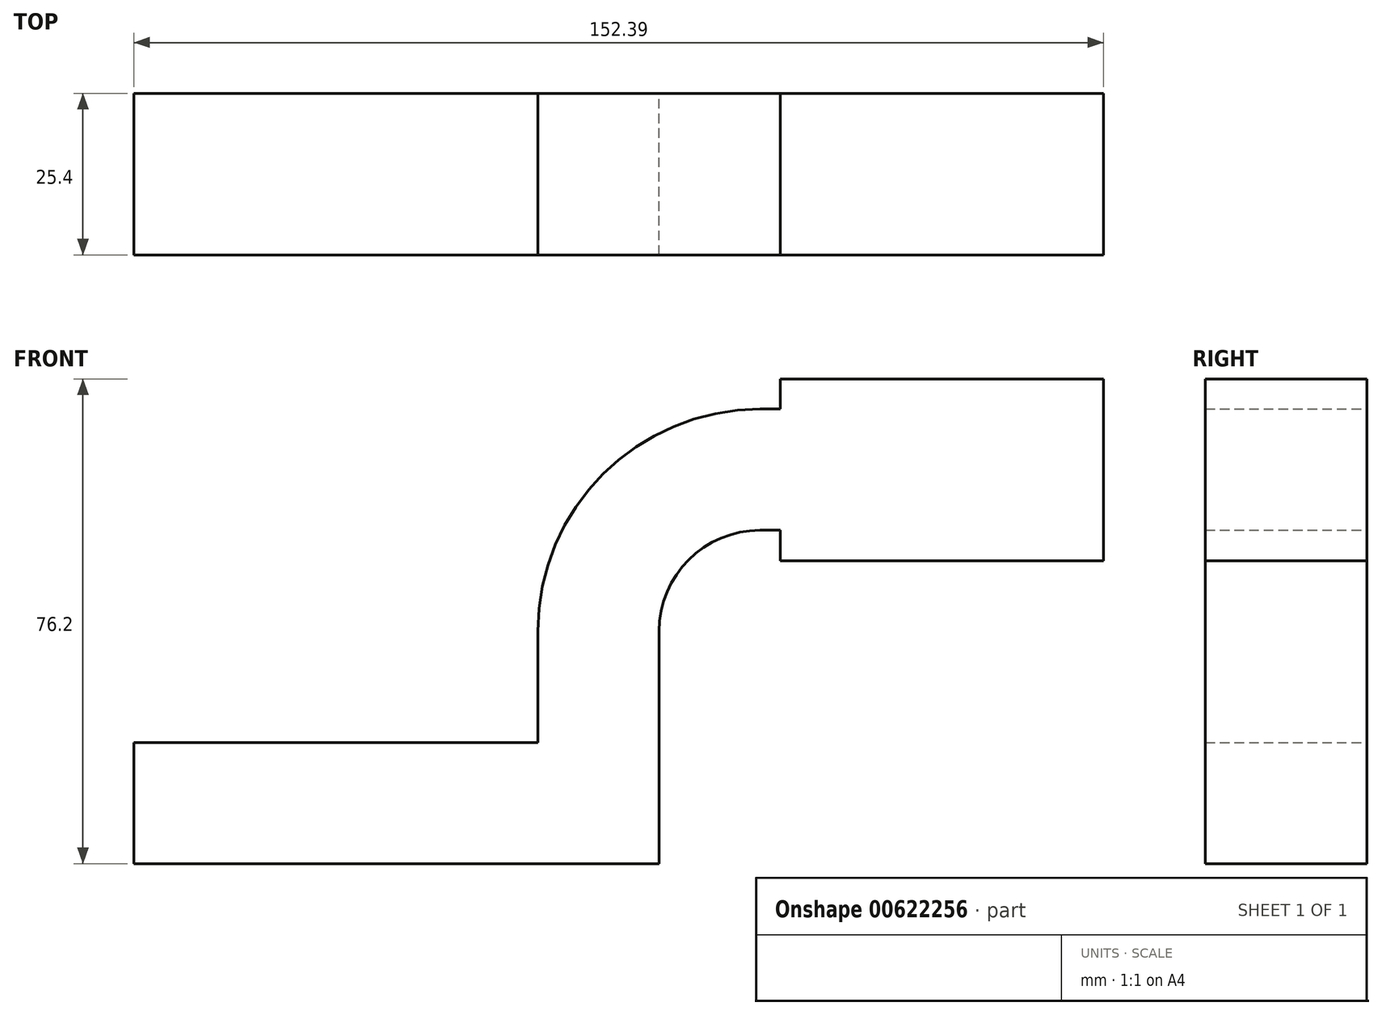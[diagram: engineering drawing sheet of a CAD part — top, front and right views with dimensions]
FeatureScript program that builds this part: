
annotation { "Feature Type Name" : "Feature", "Feature Type Description" : "" }
export const myFeature = defineFeature(function(context is Context, id is Id, definition is map)
    precondition{}
    {
        {
            var Q0;
            Q0=qCreatedBy(makeId("Front.planeOp"),FACE);
            var sketch = newSketch(context, id + "F0", { "sketchPlane" : qUnion([Q0])});
            skLineSegment(sketch, "E0.bottom", {"start": v(41.28, -9.52) * mm, "end": v(-41.28, -9.52) * mm});
            skLineSegment(sketch, "E0.top", {"start": v(41.28, 9.53) * mm, "end": v(-41.28, 9.53) * mm});
            skLineSegment(sketch, "E0.left", {"start": v(41.28, -9.52) * mm, "end": v(41.28, 9.53) * mm});
            skLineSegment(sketch, "E0.right", {"start": v(-41.28, -9.52) * mm, "end": v(-41.28, 9.53) * mm});
            skPoint(sketch, "E0.middle", {"position": v(0, 0) * mm});
            skLineSegment(sketch, "E1.bottom", {"start": v(111.12, 38.1) * mm, "end": v(60.32, 38.1) * mm});
            skLineSegment(sketch, "E1.top", {"start": v(111.12, 66.67) * mm, "end": v(60.32, 66.67) * mm});
            skLineSegment(sketch, "E1.left", {"start": v(111.12, 38.1) * mm, "end": v(111.12, 66.68) * mm});
            skLineSegment(sketch, "E1.right", {"start": v(60.32, 38.1) * mm, "end": v(60.32, 66.68) * mm});
            skPoint(sketch, "E1.middle", {"position": v(85.72, 52.39) * mm});
            skLineSegment(sketch, "E2", {"start": v(41.28, 9.53) * mm, "end": v(41.28, 27) * mm});
            skArc(sketch, "E3", {"start": v(41.28, 27) * mm, "mid": v(45.92, 38.23) * mm, "end": v(57.15, 42.88) * mm});
            skLineSegment(sketch, "E4", {"start": v(57.15, 42.88) * mm, "end": v(85.56, 42.88) * mm});
            skLineSegment(sketch, "E5.0", {"start": v(57.15, 61.93) * mm, "end": v(81.15, 61.93) * mm});
            skArc(sketch, "E5.1", {"start": v(22.23, 27) * mm, "mid": v(32.45, 51.7) * mm, "end": v(57.15, 61.93) * mm});
            skLineSegment(sketch, "E5.2", {"start": v(22.23, 9.53) * mm, "end": v(22.23, 27) * mm});
            skSolve(sketch);
        }
        {
            var Q0;
            Q0 = qSketchRegion(id + "F0", true);
            extrude(context, id + "F1", {"entities" : qUnion([Q0]), "depth" : 25.4 * mm, "offsetDistance" : 25.4 * mm});
        }
    });
